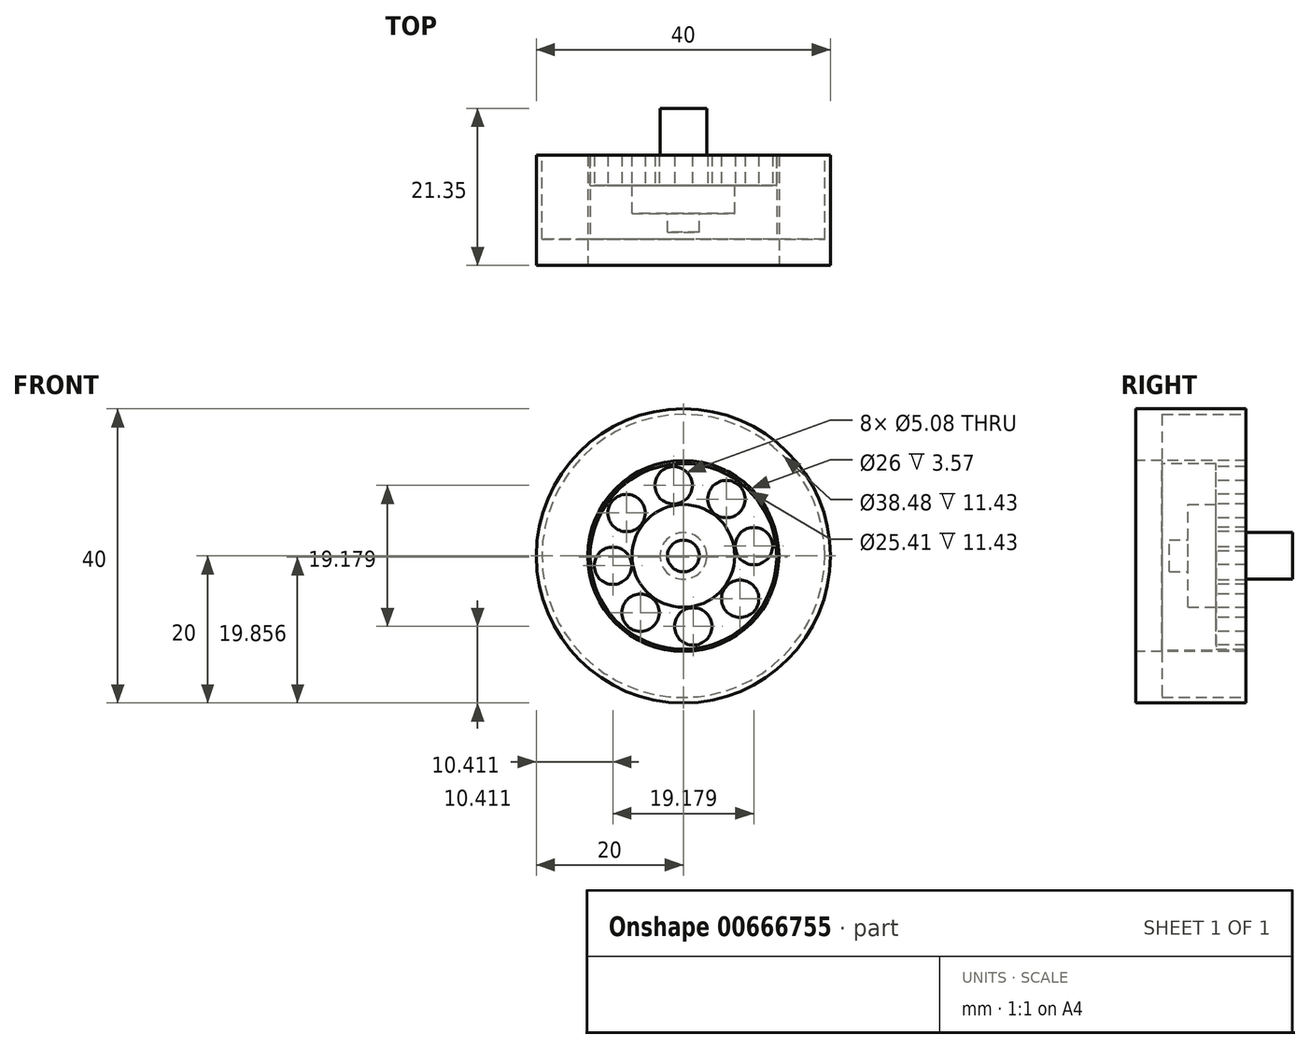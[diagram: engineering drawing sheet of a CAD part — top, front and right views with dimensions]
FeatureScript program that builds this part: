
annotation { "Feature Type Name" : "Feature", "Feature Type Description" : "" }
export const myFeature = defineFeature(function(context is Context, id is Id, definition is map)
    precondition{}
    {
        {
            var Q0;
            Q0=qCreatedBy(makeId("Front.planeOp"),FACE);
            var sketch = newSketch(context, id + "F0", { "sketchPlane" : qUnion([Q0])});
            skCircle(sketch, "E0", {"center": v(0, 0) * mm, "radius": 20 * mm});
            skCircle(sketch, "E1", {"center": v(-7.72, 5.84) * mm, "radius": 2.54 * mm});
            skCircle(sketch, "E2.1.0", {"center": v(-9.59, -1.33) * mm, "radius": 2.54 * mm});
            skCircle(sketch, "E2.2.0", {"center": v(-5.84, -7.72) * mm, "radius": 2.54 * mm});
            skCircle(sketch, "E2.3.0", {"center": v(1.33, -9.59) * mm, "radius": 2.54 * mm});
            skCircle(sketch, "E2.4.0", {"center": v(7.72, -5.84) * mm, "radius": 2.54 * mm});
            skCircle(sketch, "E2.5.0", {"center": v(9.59, 1.33) * mm, "radius": 2.54 * mm});
            skCircle(sketch, "E2.6.0", {"center": v(5.84, 7.72) * mm, "radius": 2.54 * mm});
            skCircle(sketch, "E2.7.0", {"center": v(-1.33, 9.59) * mm, "radius": 2.54 * mm});
            skSolve(sketch);
        }
        {
            var Q0;
            Q0=makeQuery(id+"F0.imprint","IMPRINT",FACE,{"disambiguationData":[TD([[makeQuery(id+"F0.imprint","IMPRINT",EDGE,{"derivedFrom":sQuery(id+"F0.wireOp",EDGE,"E0")}),1.0]])]});
            extrude(context, id + "F1", {"entities" : qUnion([Q0]), "oppositeDirection" : true, "depth" : 15 * mm, "offsetDistance" : 25.4 * mm});
        }
        {
            var Q0;
            Q0=makeQuery(id+"F0.imprint","IMPRINT",FACE,{"disambiguationData":[TD([[makeQuery(id+"F0.imprint","IMPRINT",EDGE,{"derivedFrom":sQuery(id+"F0.wireOp",EDGE,"E0")}),1.0]])]});
            var sketch = newSketch(context, id + "F2", { "sketchPlane" : qUnion([Q0])});
            skCircle(sketch, "E3", {"center": v(0, 0) * mm, "radius": 13 * mm});
            skSolve(sketch);
        }
        {
            var Q0;
            Q0 = qSketchRegion(id + "F2", true);
            extrude(context, id + "F3", {"entities" : qUnion([Q0]), "operationType" : NewBodyOperationType.REMOVE, "oppositeDirection" : true, "depth" : 10.9 * mm, "offsetDistance" : 25 * mm});
        }
        {
            var Q0;
            Q0=makeQuery(id+"F3.boolean.opBoolean","COPY",FACE,{"derivedFrom":makeQuery(id+"F3.opExtrude","CAP_FACE",FACE,{"disambiguationData":[OSD([sQuery(id+"F2.wireOp",EDGE,"E3")])],"isStart":false})});
            var sketch = newSketch(context, id + "F4", { "sketchPlane" : qUnion([Q0])});
            skCircle(sketch, "E4", {"center": v(0, 0) * mm, "radius": 6.99 * mm});
            skSolve(sketch);
        }
        {
            var Q0;
            Q0=makeQuery(id+"F4.imprint","IMPRINT",FACE,{"disambiguationData":[TD([[makeQuery(id+"F4.imprint","IMPRINT",EDGE,{"derivedFrom":sQuery(id+"F4.wireOp",EDGE,"E4")}),1.0]])]});
            extrude(context, id + "F5", {"entities" : qUnion([Q0]), "operationType" : NewBodyOperationType.ADD, "depth" : 3.8 * mm, "offsetDistance" : 25.4 * mm});
        }
        {
            var Q0;
            Q0=makeQuery(id+"F5.opExtrude","CAP_FACE",FACE,{"disambiguationData":[OSD([sQuery(id+"F4.wireOp",EDGE,"E4")])],"isStart":false});
            var sketch = newSketch(context, id + "F6", { "sketchPlane" : qUnion([Q0])});
            skCircle(sketch, "E5", {"center": v(0, 0) * mm, "radius": 2.16 * mm});
            skSolve(sketch);
        }
        {
            var Q0;
            Q0 = qSketchRegion(id + "F6", true);
            extrude(context, id + "F7", {"entities" : qUnion([Q0]), "operationType" : NewBodyOperationType.ADD, "depth" : 2.54 * mm, "offsetDistance" : 25.4 * mm});
        }
        {
            var Q0;
            Q0=makeQuery(id+"F1.opExtrude","CAP_FACE",FACE,{"disambiguationData":[OSD([sQuery(id+"F0.wireOp",EDGE,"E0"),sQuery(id+"F0.wireOp",EDGE,"E1"),sQuery(id+"F0.wireOp",EDGE,"E2.1.0"),sQuery(id+"F0.wireOp",EDGE,"E2.2.0"),sQuery(id+"F0.wireOp",EDGE,"E2.3.0"),sQuery(id+"F0.wireOp",EDGE,"E2.4.0"),sQuery(id+"F0.wireOp",EDGE,"E2.5.0"),sQuery(id+"F0.wireOp",EDGE,"E2.6.0"),sQuery(id+"F0.wireOp",EDGE,"E2.7.0")])],"isStart":false});
            var sketch = newSketch(context, id + "F8", { "sketchPlane" : qUnion([Q0])});
            skCircle(sketch, "E6", {"center": v(0, 0) * mm, "radius": 12.7 * mm});
            skCircle(sketch, "E7", {"center": v(0, 0) * mm, "radius": 19.24 * mm});
            skSolve(sketch);
        }
        {
            var Q0;
            Q0=makeQuery(id+"F8.imprint","IMPRINT",FACE,{"disambiguationData":[TD([[makeQuery(id+"F8.imprint","IMPRINT",EDGE,{"derivedFrom":sQuery(id+"F8.wireOp",EDGE,"E6")}),-1.0]])]});
            extrude(context, id + "F9", {"entities" : qUnion([Q0]), "operationType" : NewBodyOperationType.REMOVE, "oppositeDirection" : true, "depth" : 11.43 * mm, "offsetDistance" : 25.4 * mm});
        }
        {
            var Q0;
            {var subQ0=sQuery(id+"F0.wireOp",EDGE,"E2.3.0");var subQ1=sQuery(id+"F0.wireOp",EDGE,"E2.2.0");var subQ2=sQuery(id+"F0.wireOp",EDGE,"E2.1.0");var subQ3=sQuery(id+"F0.wireOp",EDGE,"E1");var subQ4=sQuery(id+"F0.wireOp",EDGE,"E2.4.0");var subQ5=sQuery(id+"F0.wireOp",EDGE,"E2.5.0");var subQ6=sQuery(id+"F0.wireOp",EDGE,"E2.6.0");var subQ7=sQuery(id+"F0.wireOp",EDGE,"E2.7.0");Q0=makeQuery(id+"F9.boolean.opBoolean","SPLIT",FACE,{"disambiguationData":[TD([makeQuery(id+"F1.opExtrude","SWEPT_FACE",FACE,{"disambiguationData":[OSD([subQ3])]})])],"derivedFrom":makeQuery(id+"F1.opExtrude","CAP_FACE",FACE,{"disambiguationData":[OSD([sQuery(id+"F0.wireOp",EDGE,"E0"),subQ3,subQ2,subQ1,subQ0,subQ4,subQ5,subQ6,subQ7])],"isStart":false})});}
            var sketch = newSketch(context, id + "F10", { "sketchPlane" : qUnion([Q0])});
            skCircle(sketch, "E8", {"center": v(0, 0) * mm, "radius": 3.17 * mm});
            skSolve(sketch);
        }
        {
            var Q0;
            Q0=makeQuery(id+"F10.imprint","IMPRINT",FACE,{"disambiguationData":[TD([[makeQuery(id+"F10.imprint","IMPRINT",EDGE,{"derivedFrom":sQuery(id+"F10.wireOp",EDGE,"E8")}),1.0]])]});
            extrude(context, id + "F11", {"entities" : qUnion([Q0]), "operationType" : NewBodyOperationType.ADD, "depth" : 6.35 * mm, "offsetDistance" : 25.4 * mm});
        }
        {
            var Q0;
            Q0=makeQuery(id+"F9.boolean.opBoolean","COPY",FACE,{"derivedFrom":makeQuery(id+"F9.opExtrude","CAP_FACE",FACE,{"disambiguationData":[OSD([sQuery(id+"F8.wireOp",EDGE,"E6"),sQuery(id+"F8.wireOp",EDGE,"E7")])],"isStart":false})});
            var sketch = newSketch(context, id + "F12", { "sketchPlane" : qUnion([Q0])});
            skCircle(sketch, "E9", {"center": v(0, 0) * mm, "radius": 12.97 * mm});
            skCircle(sketch, "E10", {"center": v(0, 0) * mm, "radius": 12.73 * mm});
            skSolve(sketch);
        }
        {
            var Q0;
            {var subQ0=sQuery(id+"F8.wireOp",EDGE,"E7");Q0=makeQuery(id+"F12.imprint","IMPRINT",FACE,{"disambiguationData":[TD([[makeQuery(id+"F12.imprint","IMPRINT",EDGE,{"derivedFrom":makeQuery(id+"F9.boolean.opBoolean","COPY",EDGE,{"derivedFrom":makeQuery(id+"F9.opExtrude","CAP_EDGE",EDGE,{"disambiguationData":[OSD([subQ0])],"isStart":false})})}),1.0]])]});}
            var sketch = newSketch(context, id + "F13", { "sketchPlane" : qUnion([Q0])});
            skCircle(sketch, "E11", {"center": v(0, 0) * mm, "radius": 13.18 * mm});
            skCircle(sketch, "E12", {"center": v(0, -0.14) * mm, "radius": 12.7 * mm});
            skSolve(sketch);
        }
        {
            var Q0;
            Q0=makeQuery(id+"F13.imprint","IMPRINT",FACE,{"disambiguationData":[TD([[makeQuery(id+"F13.imprint","IMPRINT",EDGE,{"derivedFrom":sQuery(id+"F13.wireOp",EDGE,"E12")}),-1.0]])]});
            extrude(context, id + "F14", {"entities" : qUnion([Q0]), "operationType" : NewBodyOperationType.ADD, "depth" : 11.43 * mm, "offsetDistance" : 25.4 * mm});
        }
    });
